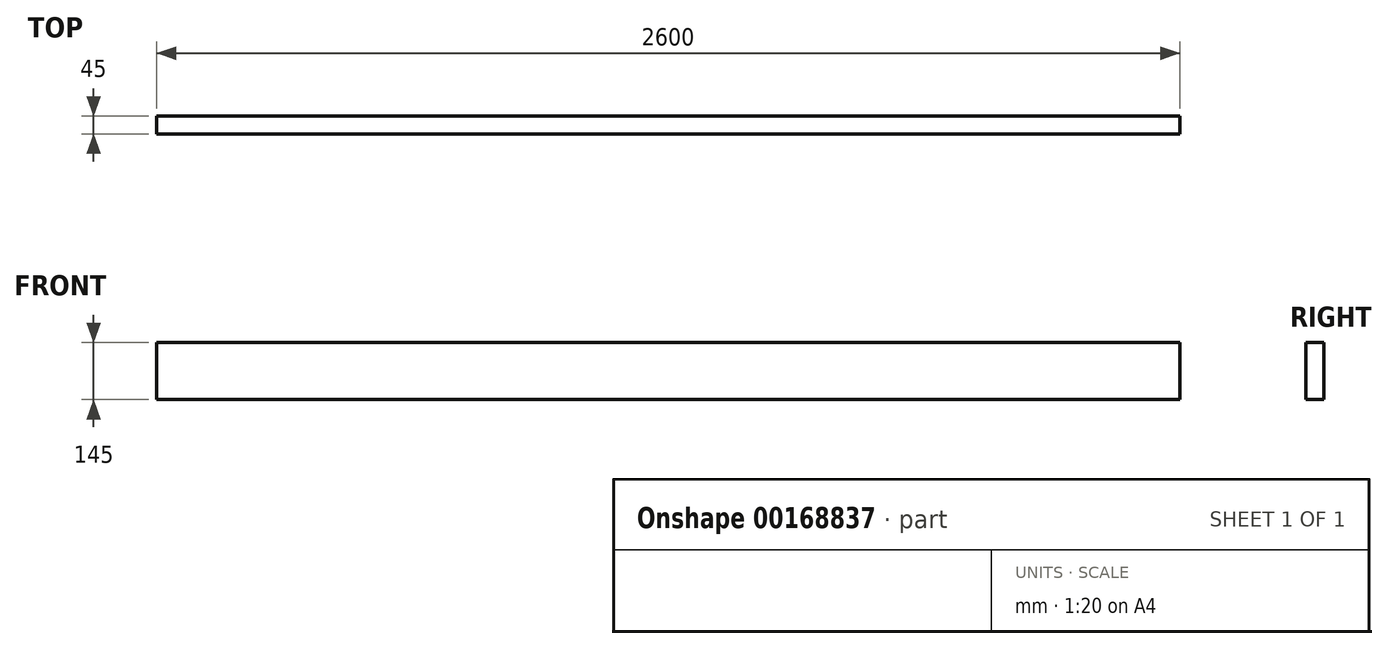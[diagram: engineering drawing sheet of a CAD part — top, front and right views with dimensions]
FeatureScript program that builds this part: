
annotation { "Feature Type Name" : "Feature", "Feature Type Description" : "" }
export const myFeature = defineFeature(function(context is Context, id is Id, definition is map)
    precondition{}
    {
        {
            var Q0;
            Q0=qCreatedBy(makeId("Right.planeOp"),FACE);
            var sketch = newSketch(context, id + "F0", { "sketchPlane" : qUnion([Q0])});
            skLineSegment(sketch, "E0.bottom", {"start": v(-22.5, 0) * mm, "end": v(22.5, 0) * mm});
            skLineSegment(sketch, "E0.top", {"start": v(-22.5, 145) * mm, "end": v(22.5, 145) * mm});
            skLineSegment(sketch, "E0.left", {"start": v(-22.5, 0) * mm, "end": v(-22.5, 145) * mm});
            skLineSegment(sketch, "E0.right", {"start": v(22.5, 0) * mm, "end": v(22.5, 145) * mm});
            skSolve(sketch);
        }
        {
            var Q0;
            Q0=makeQuery(id+"F0.imprint","IMPRINT",FACE,{"disambiguationData":[TD([[makeQuery(id+"F0.imprint","IMPRINT",EDGE,{"derivedFrom":sQuery(id+"F0.wireOp",EDGE,"E0.bottom")}),1.0]])]});
            extrude(context, id + "F1", {"entities" : qUnion([Q0]), "oppositeDirection" : true, "depth" : 2600 * mm});
        }
    });
